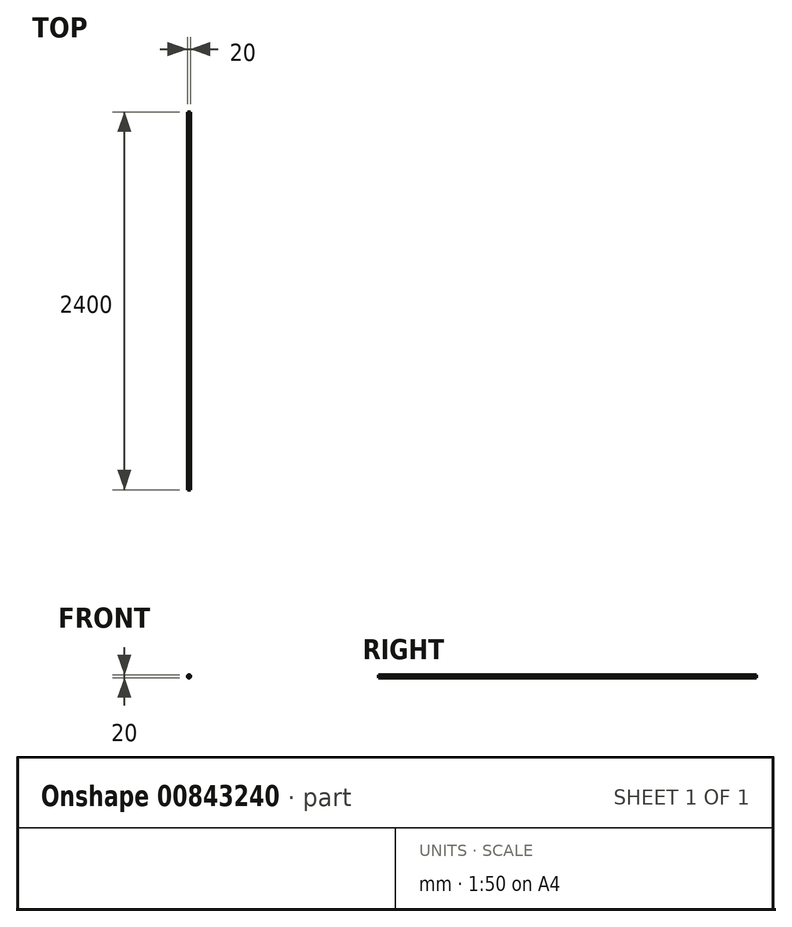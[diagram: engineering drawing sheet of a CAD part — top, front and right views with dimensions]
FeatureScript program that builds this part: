
annotation { "Feature Type Name" : "Feature", "Feature Type Description" : "" }
export const myFeature = defineFeature(function(context is Context, id is Id, definition is map)
    precondition{}
    {
        {
            var Q0;
            Q0=qCreatedBy(makeId("Front.planeOp"),FACE);
            var sketch = newSketch(context, id + "F0", { "sketchPlane" : qUnion([Q0])});
            skCircle(sketch, "E0", {"center": v(0, 0) * mm, "radius": 10 * mm});
            skSolve(sketch);
        }
        {
            var Q0;
            Q0 = qSketchRegion(id + "F0", true);
            extrude(context, id + "F1", {"entities" : qUnion([Q0]), "depth" : 2400 * mm, "offsetDistance" : 25 * mm});
        }
    });
